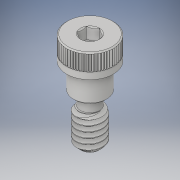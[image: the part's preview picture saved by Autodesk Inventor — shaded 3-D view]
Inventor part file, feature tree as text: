
AUTODESK INVENTOR PART (.ipt)
format: ipt  version: 2017 (Build 210142000, 142)  size: 596,480 bytes
history: mixed  units: in
note: dims shown in document units (in); Inventor stores cm internally (conversion verified against a paired STEP export)
features: chamfer x1, imported_body x1
ambient origin geometry x8: Origin, YZ Plane, XZ Plane, XY Plane, X Axis, Y Axis, Z Axis, Center Point
bodies: Solid1 (imported_parasolid)
feature tree (2):
  chamfer  "Chamfer3"  [1 undecoded]
  imported_body  NMx_Import_Brep_tag  [imported B-rep: ~22 faces, bbox_mm=[5.548635, 11.90625, 9.101667]]
note: 1 required parameter value undecoded (feature->parameter linkage not recoverable at this tier; creation-order binding heuristic only, values carry confidence <= 0.55)
